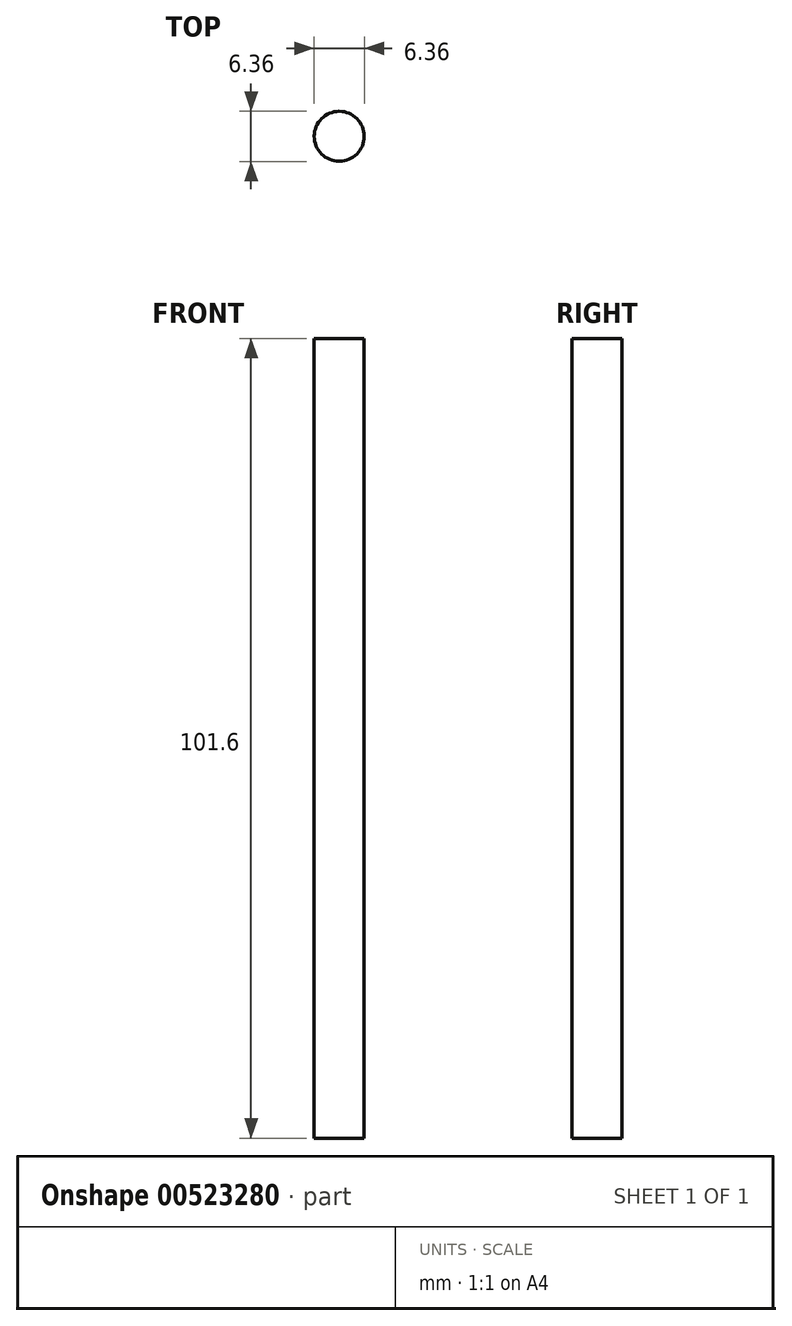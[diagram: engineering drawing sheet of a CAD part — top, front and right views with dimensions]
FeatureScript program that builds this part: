
annotation { "Feature Type Name" : "Feature", "Feature Type Description" : "" }
export const myFeature = defineFeature(function(context is Context, id is Id, definition is map)
    precondition{}
    {
        {
            var Q0;
            Q0=qCreatedBy(makeId("Top.planeOp"),FACE);
            var sketch = newSketch(context, id + "F0", { "sketchPlane" : qUnion([Q0])});
            skCircle(sketch, "E0", {"center": v(0, 0) * mm, "radius": 3.18 * mm});
            skSolve(sketch);
        }
        {
            var Q0;
            Q0=makeQuery(id+"F0.imprint","IMPRINT",FACE,{"disambiguationData":[TD([[makeQuery(id+"F0.imprint","IMPRINT",EDGE,{"derivedFrom":sQuery(id+"F0.wireOp",EDGE,"E0")}),1.0]])]});
            extrude(context, id + "F1", {"entities" : qUnion([Q0]), "depth" : 101.6 * mm, "offsetDistance" : 25.4 * mm});
        }
    });
